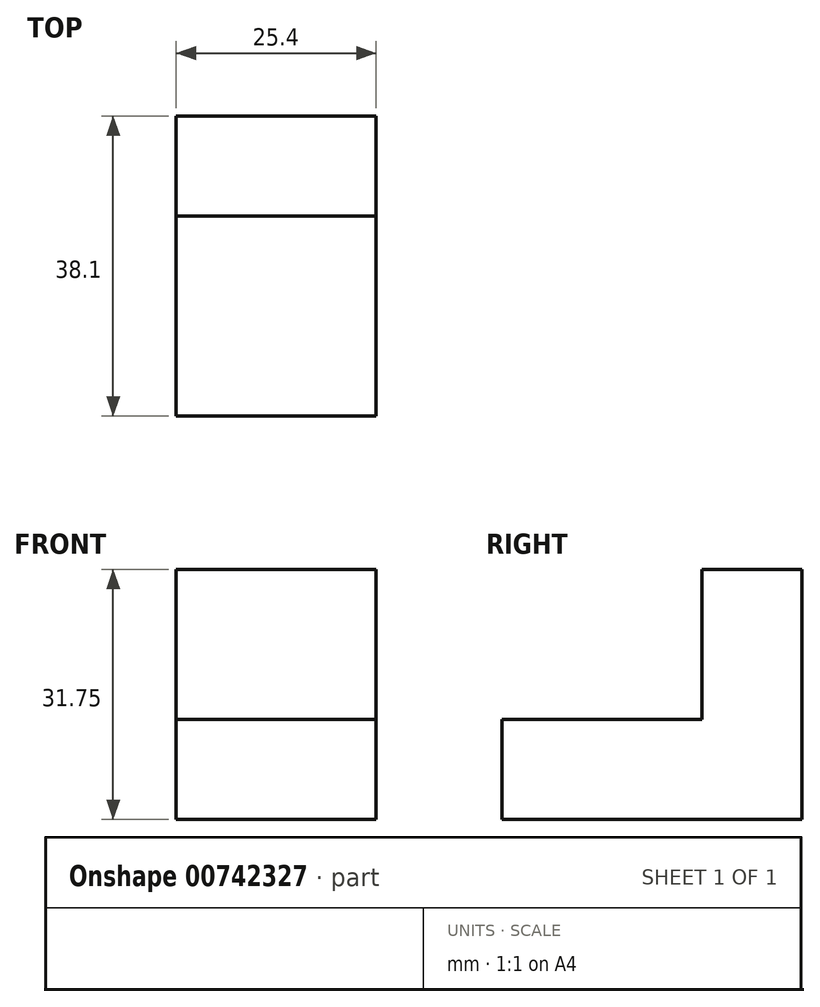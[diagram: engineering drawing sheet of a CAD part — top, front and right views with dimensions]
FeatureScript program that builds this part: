
annotation { "Feature Type Name" : "Feature", "Feature Type Description" : "" }
export const myFeature = defineFeature(function(context is Context, id is Id, definition is map)
    precondition{}
    {
        {
            var Q0;
            Q0=qCreatedBy(makeId("Right.planeOp"),FACE);
            var sketch = newSketch(context, id + "F0", { "sketchPlane" : qUnion([Q0])});
            skLineSegment(sketch, "E0", {"start": v(0, 0) * mm, "end": v(-38.1, 0) * mm});
            skLineSegment(sketch, "E1", {"start": v(-38.1, 0) * mm, "end": v(-38.1, 12.7) * mm});
            skLineSegment(sketch, "E2", {"start": v(-38.1, 12.7) * mm, "end": v(-12.7, 12.7) * mm});
            skLineSegment(sketch, "E3", {"start": v(-12.7, 12.7) * mm, "end": v(-12.7, 31.75) * mm});
            skLineSegment(sketch, "E4", {"start": v(-12.7, 31.75) * mm, "end": v(0, 31.75) * mm});
            skLineSegment(sketch, "E5", {"start": v(0, 31.75) * mm, "end": v(0, 0) * mm});
            skSolve(sketch);
        }
        {
            var Q0;
            Q0 = qSketchRegion(id + "F0", true);
            extrude(context, id + "F1", {"entities" : qUnion([Q0]), "depth" : 25.4 * mm, "offsetDistance" : 25.4 * mm});
        }
    });
